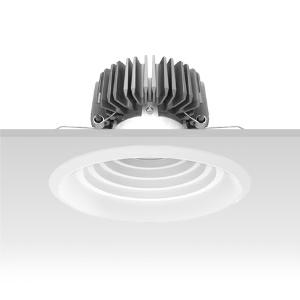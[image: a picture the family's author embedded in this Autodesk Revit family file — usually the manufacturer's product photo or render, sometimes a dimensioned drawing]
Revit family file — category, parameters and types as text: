
# Revit family: 3f_filippi_-_3f_reno_bianco_ampio_3f_filippi_-_30687_-_3f_reno_200_wh_4000-840_dali_wide
name_source: partatom
category: Lighting Fixtures
units: mm (PartAtom-declared; Revit-internal decimal feet)

## family parameters
Cut with Voids When Loaded = No
Host = Face
Light Source = No
Part Type = Normal
Room Calculation Point = No
Round Connector Dimension = Use Diameter
Shared = No

## types (1)
- 3F Filippi - 3F Reno Bianco Ampio (1 x LED, 3521 lm, 36 W, 4000 K)
    Apparent Load = 36 VA
    Approval mark = CE
    CIE Flux Codes = 80 97 100 100 100
    Color Rendering = 80
    Color Temperature = 4000 K
    Control Gear = Electronic transformer
    Default Elevation = 1800 mm
    Description = ILLUMINOTECHNICAL
Luminous efficiency 100% (DLOR 100%, ULOR 0%).
Initial luminous flux of the luminaire 3521 lm.
Direct symmetric wide distribution.
Installation Interdistance Transv.D = 1.56 x hu - Long.D = 1.56 x hu.
Tabular UGR (CIE 117 - 4H-8H; S=0.25H; 70/50/20): RUG 21.4 - 21.4.
Beam angle: 85° - 84°.
Luminous efficacy 98 lm/W.
Lifetime (L90/B10): 30000 h. (tq+25°C)
Lifetime (L85/B10): 50000 h. (tq+25°C)
Lifetime (L70/B10): 80000 h. (tq+25°C)
Sudden decreased luminous flux after 50000 hours: 0% (C0).
Photobiological safety in compliance with IEC/TR 62778: RG1 low risk, (IEC 62471).
In compliance with IEC/EN 62722-2-1 - IEC/EN 62717 standards.

SOURCE
Compact LED module 4000/840.
Energy efficiency class (UE 2019/2020 - UE 2019/2015): D.
CIE 13.3 Colour rendering index: CRI >80 (R9 <50%).
IES TM-30 Fidelity Index: Rf = 84 Rg = 95.
CCT nominal colour temperature 4000 K.
Colour initial tolerance (MacAdam): SDCM 3.
Zhaga Book 3 compliant.

MECHANICAL
Passive heat dissipator in die-casting aluminium, oversized, for optimum thermal management of the LED module.
Parabolic element with graduated/concentric rings in white polycarbonate.
Transparent external lens with glossy and satin differentiated surfaces, with a cooling and anti-insect system in methacrylate (PMMA).
Fastening spring clips in stainless steel.
Dimensions: diameter 216 mm, height 142 mm. Weight 1.5 kg.
IP44 protection degree for exposed part, IP20 for recessed part.
Mechanical strength to impacts IK04 (0.5 joule).
Glow-wire test resistance 650°C.

ELECTRICAL
Wiring on a separate unit.
Halogen Free DALI-2 DATI (Parts 251, 252, 253), PUSH-DIM, electronic wiring 230V-50/60Hz, power factor 0.97 at full load, THD <25%, constant output current, SELV, class II, 1 driver, 1 DALI addresse.
Power of the luminaire 36 W.
ENEC - CE.
SAFE FLICKER: PstLM=<1 and SVM=<0.4 (IEC TR 61547-1 and IEC TR 63158), to ensure a more comfortable and safe light.
Luminaire compliant with EN 60598-2-22 for power supply from a centralised emergency system CPSS (Central Power Supply System), not incorporated in the luminaire - high risk areas excluded. The default power and flux are 100% in AC and 100% in DC.
Ambient temperature from 0°C to +25°C.
Temperature class T6 max 85°C.
Relative humidity UR: <85%.

INSTALLATION
Pull-up recessed fitting.
False ceiling carving: 200 mm.
All accessories dedicated to this product are available on the Catalog and on our website www.3F-Filippi.com.

APPLICATIONS
Environments: architectural, commercial, exhibition areas, transit areas, corridors, shops, display windows, service areas.
In false ceilings with narrow voids.

LIGHT MANAGEMENT
Recommended minimum setting: 10%.
The luminaire, equipped with (DALI-2 DATI) driver, can be controlled manually with 3F Easy Dim technology or automatically/manually with wired or wireless DALI/D2D control systems.
The D2D driver guarantees interoperability with other devices with the same certification by making the following information available:
Device Data (Part 251), Energy Report (Part 252), Diagnosis & Maintenance (Part 253).
In electrical systems without a regulation system (manual or automatic) and DALI bus, a suitable jumper must be made on the DA-DA terminals of the appliance.

WARNING
Luminaire designed for disposal/recycling at end-of-life.
Replaceable (LED only) light source by a professional. Replaceable control gear by a professional.
    Height = 0 mm  [stored 0 ft]
    Lamp = 1 x LED
    Lamp Light Flux = 3521 lm
    Lamp Power = 36 W
    Lamp count = 1
    Length = 216 mm
    Lifetime = 50000 h
    Luminous efficacy = 98 lm/W
    Manufacturer = 3F Filippi
    ModVariant = No
    Model = 3F Filippi - 30687 - 3F Reno 200 WH 4000-840 DALI WIDE
    Mounting Place = Ceiling
    Mounting Type = Recessed
    Number of Poles = 1
    OnlyDefault = Yes
    Power Factor = 1
    Product Name = 3F Filippi - 3F Reno Bianco Ampio
    Product group = recessed luminaire
    ProductGroupID = 4
    Protection Class = Protection class II
    Protection Degree = IP 20
    RLX_Detail_Level = 1
    RLX_Emergency_Light_Flux = 0 lm
    RLX_Emergency_Type = 0
    RLX_Emergency_Type_DB = No
    RlxData = <blob elided: 95133 chars, md5=f7470df3>
    Socket = socket
    Standby Power = 0 W
    System Light Flux = 3521 lm
    System Power = 36 W
    Type Comments = Product without accessories
    Type Image = 3ffilippi_3f_reno_200_wh_2500_3000_4000.jpg
    URL = http://relux.com
    VarID = ---
    Voltage = 0 V
    Weight = 0.00 kg
    Width = 0 mm  [stored 0 ft]

note: [stored X ft] marks values corroborated as IEEE doubles in the binary element streams (Revit-internal decimal feet)

## geometry (parser evidence)
native form markers: Blend x4, Sweep x9
no freeform markers — native parametric forms only
